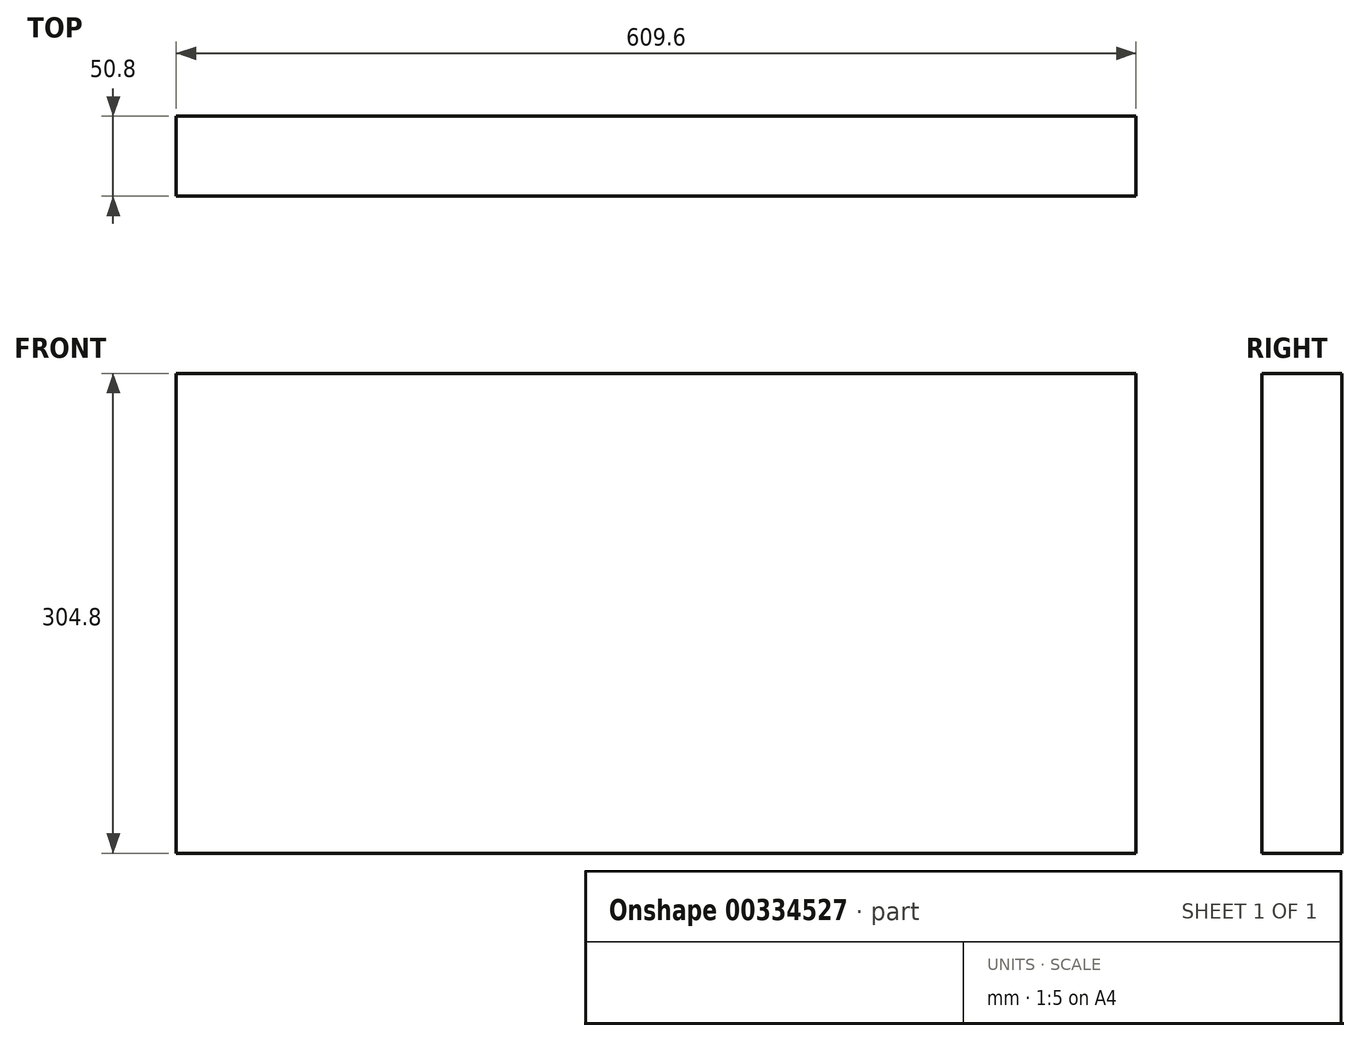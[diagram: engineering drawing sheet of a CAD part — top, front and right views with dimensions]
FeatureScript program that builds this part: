
annotation { "Feature Type Name" : "Feature", "Feature Type Description" : "" }
export const myFeature = defineFeature(function(context is Context, id is Id, definition is map)
    precondition{}
    {
        {
            var Q0;
            Q0=qCreatedBy(makeId("Front.planeOp"),FACE);
            var sketch = newSketch(context, id + "F0", { "sketchPlane" : qUnion([Q0])});
            skLineSegment(sketch, "E0.bottom", {"start": v(-297.26, 147.68) * mm, "end": v(312.34, 147.68) * mm});
            skLineSegment(sketch, "E0.top", {"start": v(-297.26, -157.12) * mm, "end": v(312.34, -157.12) * mm});
            skLineSegment(sketch, "E0.left", {"start": v(-297.26, 147.68) * mm, "end": v(-297.26, -157.12) * mm});
            skLineSegment(sketch, "E0.right", {"start": v(312.34, 147.68) * mm, "end": v(312.34, -157.12) * mm});
            skSolve(sketch);
        }
        {
            var Q0;
            Q0 = qSketchRegion(id + "F0", true);
            extrude(context, id + "F1", {"entities" : qUnion([Q0]), "depth" : 50.8 * mm});
        }
    });
